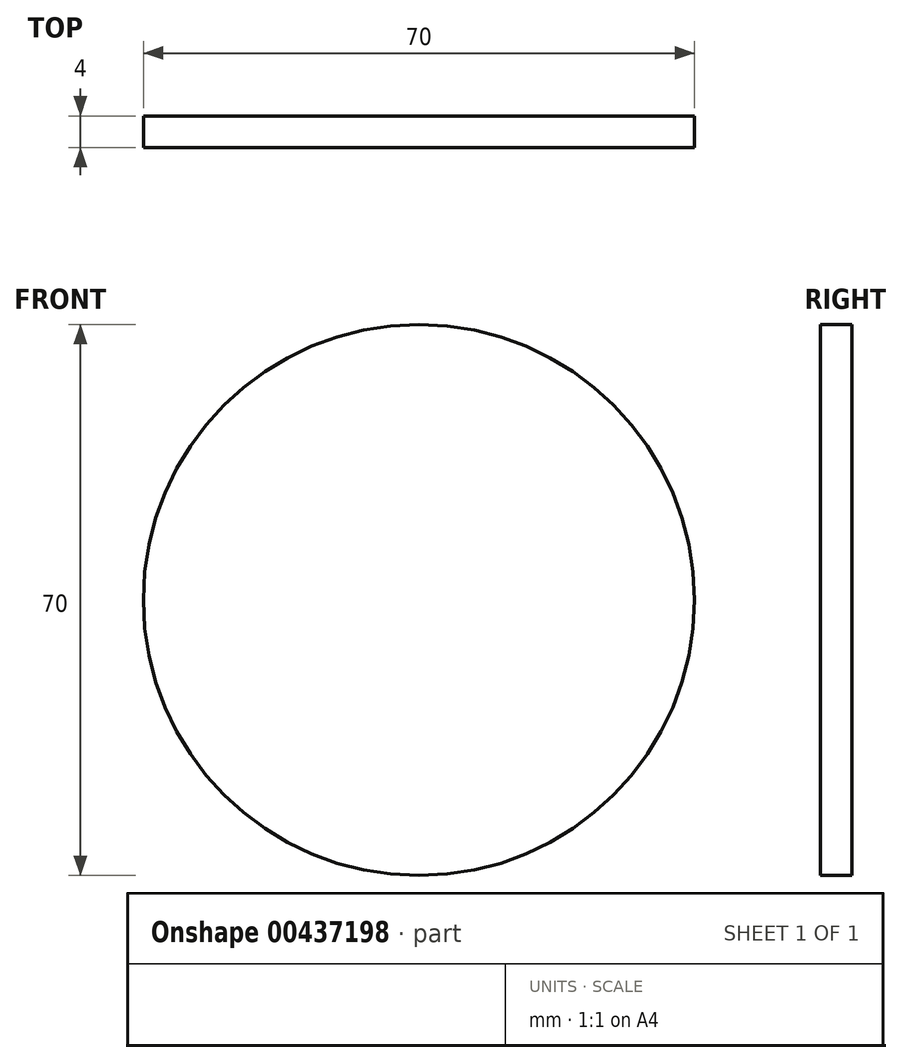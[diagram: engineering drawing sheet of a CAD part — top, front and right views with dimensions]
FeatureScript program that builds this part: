
annotation { "Feature Type Name" : "Feature", "Feature Type Description" : "" }
export const myFeature = defineFeature(function(context is Context, id is Id, definition is map)
    precondition{}
    {
        {
            var Q0;
            Q0=qCreatedBy(makeId("Front.planeOp"),FACE);
            var sketch = newSketch(context, id + "F0", { "sketchPlane" : qUnion([Q0])});
            skCircle(sketch, "E0", {"center": v(0, 0) * mm, "radius": 35 * mm});
            skSolve(sketch);
        }
        {
            var Q0;
            Q0 = qSketchRegion(id + "F0", true);
            extrude(context, id + "F1", {"entities" : qUnion([Q0]), "depth" : 4 * mm});
        }
    });
